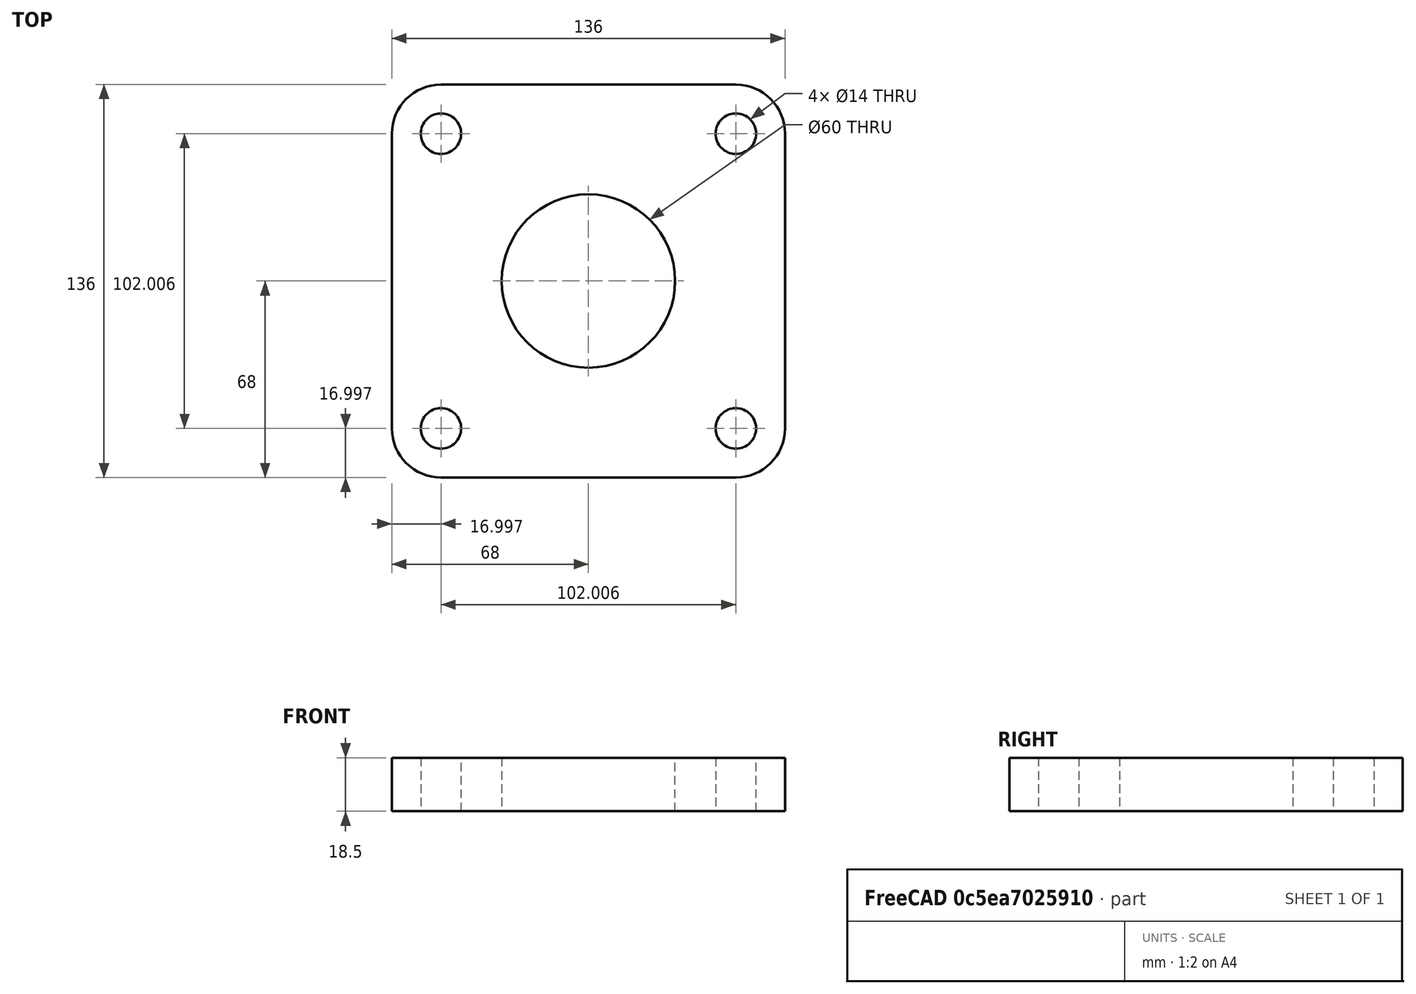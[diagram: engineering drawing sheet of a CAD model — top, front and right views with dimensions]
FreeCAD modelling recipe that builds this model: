
FCSTD DOCUMENT  (FreeCAD 0.20R29177 +426 (Git))
Label: PillowBlockSpacer
License: All rights reserved
LicenseURL: http://en.wikipedia.org/wiki/All_rights_reserved
objects: PartDesign::CoordinateSystem×1, Sketcher::SketchObject×1, PartDesign::Pad×1, PartDesign::Body×1
note: 5 computed .brp shape members not serialized (recipe doc carries the construction recipe); baked Part::Feature solids carry a one-line shape summary decoded from their .brp
EXTERNAL_REF file=Params.FCStd obj=Spreadsheet

FEATURE [PartDesign::CoordinateSystem] LCS_0
  AttacherType = Attacher::AttachEngine3D
  MapMode = 2
  Support = -> [X_Axis]
FEATURE [Sketcher::SketchObject] Sketch001
  FullyConstrained = true
  MapMode = 5
  Support = -> [XY_Plane]
  sketch-geometry (15):
    g0: ArcOfCircle CenterX=-51.0032 CenterY=51.0032 CenterZ=0 NormalX=0 NormalY=0 NormalZ=1 AngleXU=0 Radius=16.9968 StartAngle=1.5708 EndAngle=3.14159
    g1: LineSegment StartX=-51.0032 StartY=68 StartZ=0 EndX=51.0032 EndY=68 EndZ=0
    g2: ArcOfCircle CenterX=51.0032 CenterY=51.0032 CenterZ=0 NormalX=0 NormalY=0 NormalZ=1 AngleXU=0 Radius=16.9968 StartAngle=-1.226e-13 EndAngle=1.5708
    g3: LineSegment StartX=68 StartY=51.0032 StartZ=0 EndX=68 EndY=-51.0032 EndZ=0
    g4: ArcOfCircle CenterX=51.0032 CenterY=-51.0032 CenterZ=0 NormalX=0 NormalY=0 NormalZ=1 AngleXU=0 Radius=16.9968 StartAngle=4.71239 EndAngle=6.28319
    g5: LineSegment StartX=51.0032 StartY=-68 StartZ=0 EndX=-51.0032 EndY=-68 EndZ=0
    g6: ArcOfCircle CenterX=-51.0032 CenterY=-51.0032 CenterZ=0 NormalX=0 NormalY=0 NormalZ=1 AngleXU=0 Radius=16.9968 StartAngle=3.14159 EndAngle=4.71239
    g7: LineSegment StartX=-68 StartY=-51.0032 StartZ=0 EndX=-68 EndY=51.0032 EndZ=0
    g8: GeomPoint X=-68 Y=68 Z=0
    g9: GeomPoint X=68 Y=-68 Z=0
    g10: Circle CenterX=51.0032 CenterY=51.0032 CenterZ=0 NormalX=0 NormalY=0 NormalZ=1 AngleXU=0 Radius=7
    g11: Circle CenterX=-51.0032 CenterY=51.0032 CenterZ=0 NormalX=0 NormalY=0 NormalZ=1 AngleXU=0 Radius=7
    g12: Circle CenterX=-51.0032 CenterY=-51.0032 CenterZ=0 NormalX=0 NormalY=0 NormalZ=1 AngleXU=0 Radius=7
    g13: Circle CenterX=51.0032 CenterY=-51.0032 CenterZ=0 NormalX=0 NormalY=0 NormalZ=1 AngleXU=0 Radius=7
    g14: Circle CenterX=0 CenterY=0 CenterZ=0 NormalX=0 NormalY=0 NormalZ=1 AngleXU=0 Radius=30
  constraints (33):
    c: Tangent(g0,g1) = 1.5708
    c: Tangent(g1,g2) = 1.5708
    c: Tangent(g2,g3) = 1.5708
    c: Tangent(g3,g4) = 1.5708
    c: Tangent(g4,g5) = 1.5708
    c: Tangent(g5,g6) = 1.5708
    c: Tangent(g6,g7) = 1.5708
    c: Tangent(g7,g0) = 1.5708
    c: Horizontal(g1)
    c: Horizontal(g5)
    c: Vertical(g3)
    c: Vertical(g7)
    c: Equal(g0,g2)
    c: Equal(g2,g4)
    c: Equal(g4,g6)
    c: PointOnObject(g8,g1)
    c: PointOnObject(g8,g7)
    c: PointOnObject(g9,g3)
    c: PointOnObject(g9,g5)
    c: Equal(g1,g3)
    c: Symmetric(g2,g6,g-1)
    c: DistanceY(g4,g2) = 102.006
    c: Coincident(g10,g2)
    c: Coincident(g11,g0)
    c: Coincident(g12,g6)
    c: Coincident(g13,g4)
    c: Equal(g13,g12)
    c: Equal(g12,g11)
    c: Equal(g11,g10)
    c: Diameter(g10) = 14
    c: DistanceY(g4,g1) = 136
    c: Coincident(g14,g-1)
    c: Radius(g14) = 30
FEATURE [PartDesign::Pad] Pad
  Direction = (0,0,1)
  Length = 18.5
  Length2 = 10
  Profile = -> Sketch001
  ReferenceAxis = -> Sketch001 [N_Axis]
  Type = 0
  expr: Length = <<Params>>#<<Params>>.PlywoodThickness
FEATURE [PartDesign::Body] Body
  Group = -> [LCS_0,Sketch001,Pad]
  Origin = -> Origin
  Tip = -> Pad
